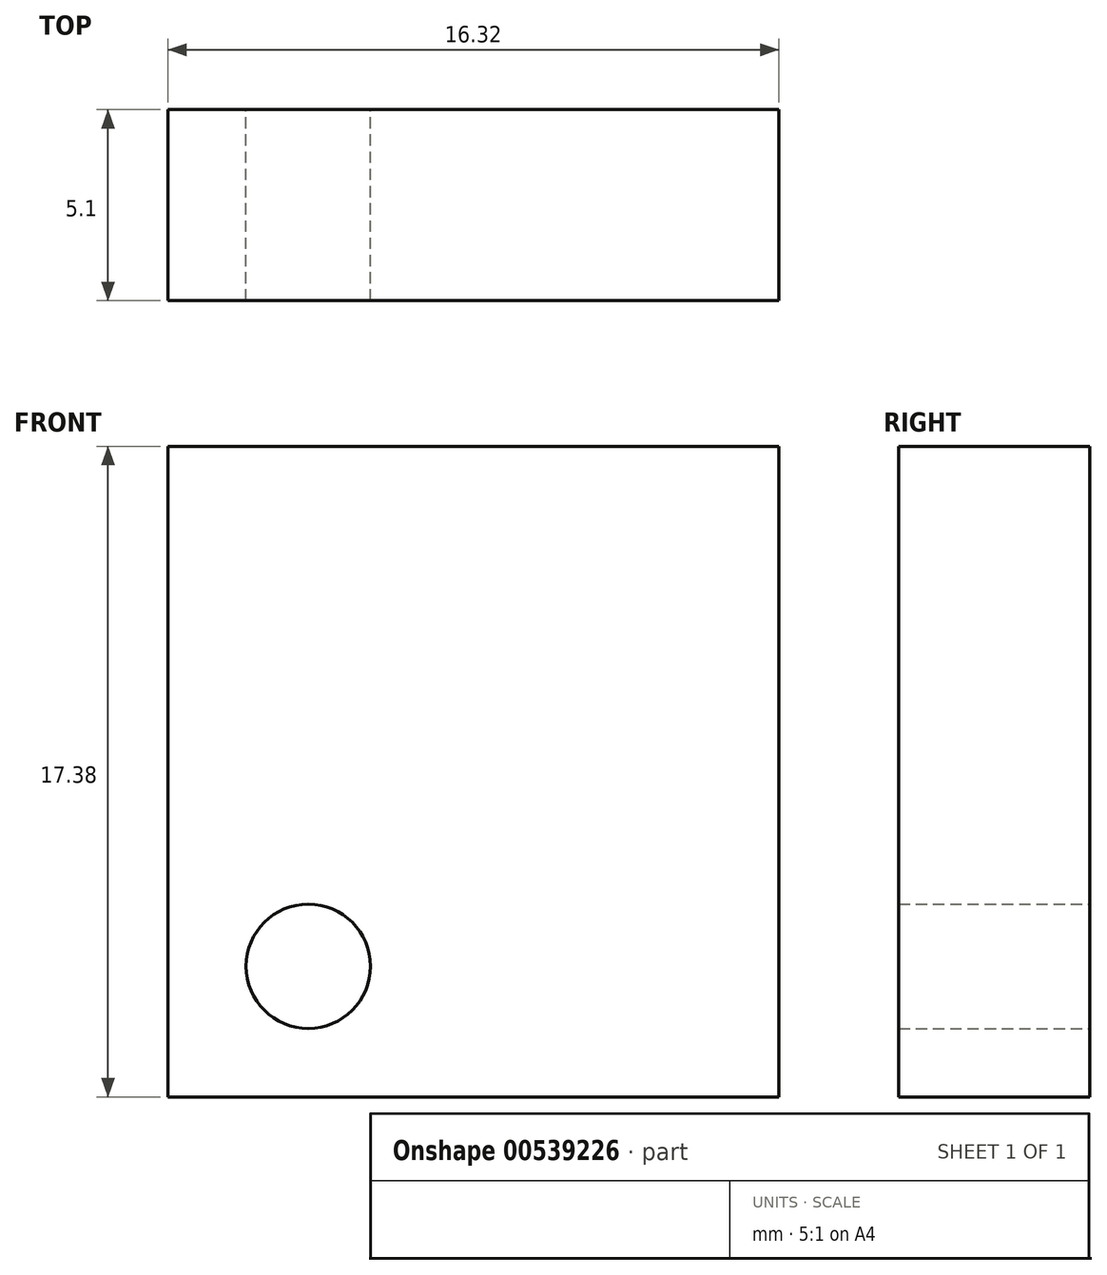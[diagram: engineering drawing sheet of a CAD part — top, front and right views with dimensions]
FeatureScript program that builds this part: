
annotation { "Feature Type Name" : "Feature", "Feature Type Description" : "" }
export const myFeature = defineFeature(function(context is Context, id is Id, definition is map)
    precondition{}
    {
        {
            var Q0;
            Q0=qCreatedBy(makeId("Front.planeOp"),FACE);
            var sketch = newSketch(context, id + "F0", { "sketchPlane" : qUnion([Q0])});
            skLineSegment(sketch, "E0.bottom", {"start": v(0, 0) * mm, "end": v(16.32, 0) * mm});
            skLineSegment(sketch, "E0.top", {"start": v(0, -17.38) * mm, "end": v(16.32, -17.38) * mm});
            skLineSegment(sketch, "E0.left", {"start": v(0, 0) * mm, "end": v(0, -17.38) * mm});
            skLineSegment(sketch, "E0.right", {"start": v(16.32, 0) * mm, "end": v(16.32, -17.38) * mm});
            skCircle(sketch, "E1", {"center": v(12.14, 8.6) * mm, "radius": 1.61 * mm});
            skCircle(sketch, "E2", {"center": v(3.75, -13.9) * mm, "radius": 1.66 * mm});
            skSolve(sketch);
        }
        {
            var Q0;
            Q0=makeQuery(id+"F0.imprint","IMPRINT",FACE,{"disambiguationData":[TD([[makeQuery(id+"F0.imprint","IMPRINT",EDGE,{"derivedFrom":sQuery(id+"F0.wireOp",EDGE,"E0.bottom")}),-1.0]])]});
            extrude(context, id + "F1", {"entities" : qUnion([Q0]), "depth" : 5.1 * mm, "offsetDistance" : 25 * mm});
        }
    });
